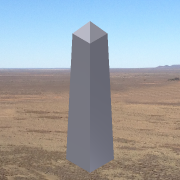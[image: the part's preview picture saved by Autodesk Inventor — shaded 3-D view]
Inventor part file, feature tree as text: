
AUTODESK INVENTOR PART (.ipt)
format: ipt  version: 2013 SP2 (Build 170200200, 200)  size: 158,720 bytes
history: native  units: in
note: dims shown in document units (in); Inventor stores cm internally (conversion verified against a paired STEP export)
features: plane x4, split x4, extrude x3, sketch x3, pattern_circular x1
ambient origin geometry x8: Origin, YZ Plane, XZ Plane, XY Plane, X Axis, Y Axis, Z Axis, Center Point
bodies: Solid1 (feature_tree)
feature tree (15):
  extrude  "Extrusion1"  Depth=1.0in TaperAngle=0.0deg
  extrude  "Extrusion2"  Depth=661.5in
  plane  "Work Plane5"
  split  "Split5"
  plane  "Work Plane6"
  split  "Split6"
  extrude  "Extrusion4"  [1 undecoded]
  plane  "Work Plane7"
  split  "Split7"
  plane  "Work Plane8"
  split  "Split8"
  pattern_circular  "Circular Pattern2"  [2 undecoded]
  sketch  "Sketch1"  dims[d0=100.0in d1=1.0in d2=0.0in]
  sketch  "Sketch2"  dims[d3=661.5in d4=661.5in]
  sketch  "Sketch4"  dims[d5=6000.0in d6=0.0in d16=-0.0117in d17=-0.0117in d18=660.0in d19=0.0in d20=-0.268in d21=-0.268in d22=1.5748in d23=360.0deg]
note: 3 required parameter values undecoded (feature->parameter linkage not recoverable at this tier; creation-order binding heuristic only, values carry confidence <= 0.55)
